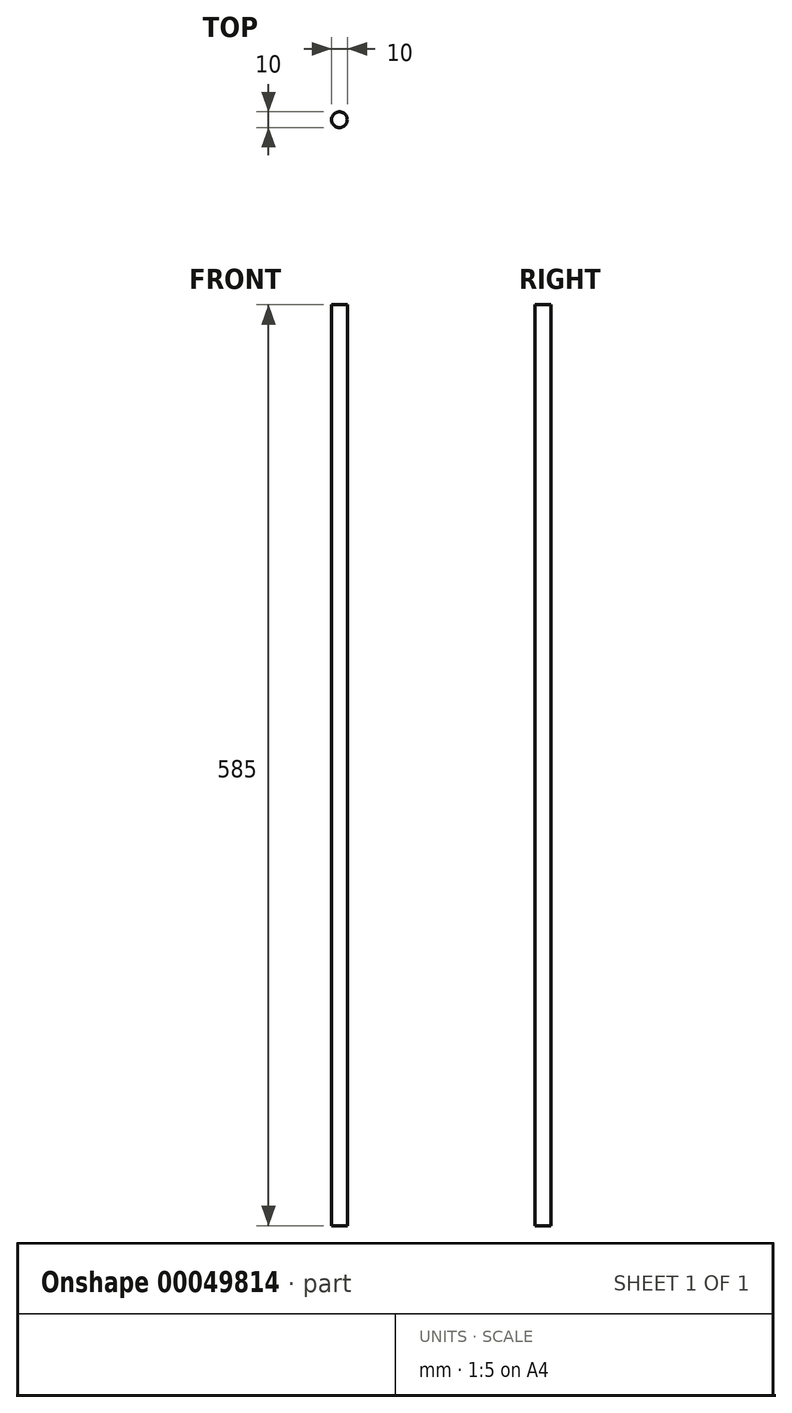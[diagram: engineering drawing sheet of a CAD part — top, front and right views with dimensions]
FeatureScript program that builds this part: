
annotation { "Feature Type Name" : "Feature", "Feature Type Description" : "" }
export const myFeature = defineFeature(function(context is Context, id is Id, definition is map)
    precondition{}
    {
        {
            var Q0;
            Q0=qCreatedBy(makeId("Top.planeOp"),FACE);
            var sketch = newSketch(context, id + "F0", { "sketchPlane" : qUnion([Q0])});
            skCircle(sketch, "E0", {"center": v(0, 0) * mm, "radius": 5 * mm});
            skSolve(sketch);
        }
        {
            var Q0;
            Q0=qSketchRegion(id+"F0",true);
            extrude(context, id + "F1", {"entities" : qUnion([Q0]), "depth" : 585 * mm});
        }
    });
